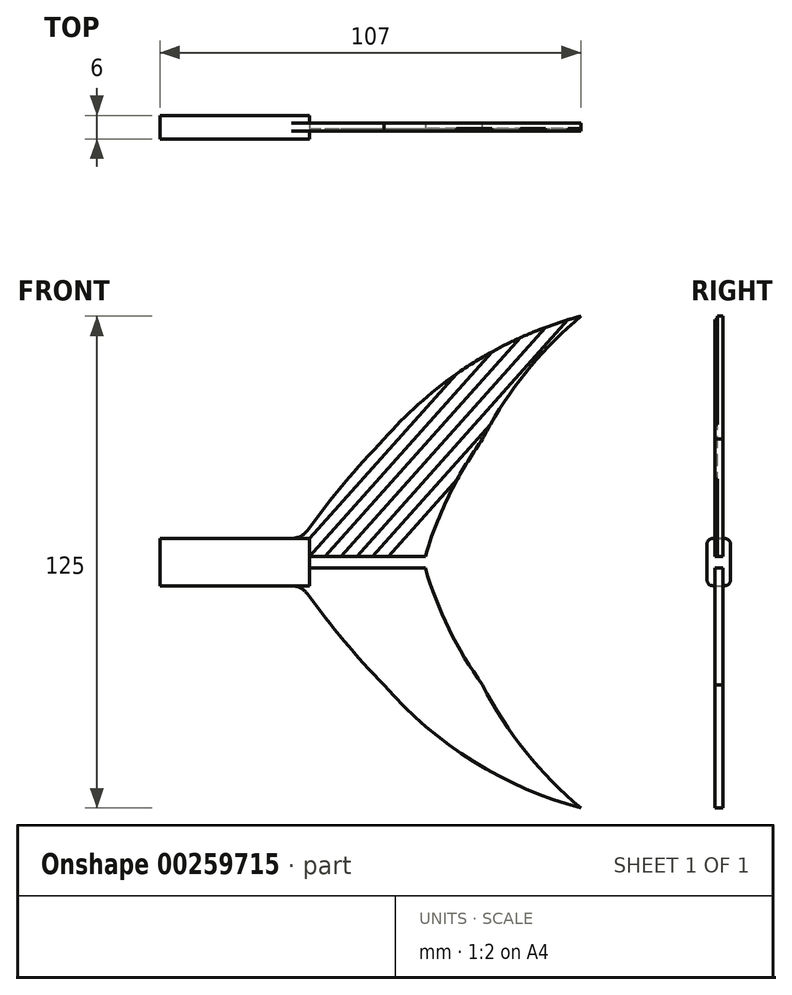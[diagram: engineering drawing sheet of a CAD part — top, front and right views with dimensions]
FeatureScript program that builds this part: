
annotation { "Feature Type Name" : "Feature", "Feature Type Description" : "" }
export const myFeature = defineFeature(function(context is Context, id is Id, definition is map)
    precondition{}
    {
        {
            var Q0;
            Q0=qCreatedBy(makeId("Front.planeOp"),FACE);
            var sketch = newSketch(context, id + "F0", { "sketchPlane" : qUnion([Q0])});
            skLineSegment(sketch, "E0", {"start": v(0, 0) * mm, "end": v(35, 0) * mm});
            skLineSegment(sketch, "E1", {"start": v(25, 31.25) * mm, "end": v(50, 31.25) * mm});
            skPoint(sketch, "E2", {"position": v(75, 62.5) * mm});
            skArc(sketch, "E3", {"start": v(25, 31.25) * mm, "mid": v(11.72, 16.25) * mm, "end": v(0, 0) * mm});
            skArc(sketch, "E4", {"start": v(75, 62.5) * mm, "mid": v(47.64, 50.64) * mm, "end": v(25, 31.25) * mm});
            skArc(sketch, "E5", {"start": v(75, 62.5) * mm, "mid": v(60.92, 48.14) * mm, "end": v(50, 31.25) * mm});
            skArc(sketch, "E6", {"start": v(50, 31.25) * mm, "mid": v(41.14, 16.28) * mm, "end": v(35, 0) * mm});
            skSolve(sketch);
        }
        {
            var Q0;
            Q0=qSketchRegion(id+"F0",true);
            extrude(context, id + "F1", {"entities" : qUnion([Q0]), "endBound" : BoundingType.SYMMETRIC, "depth" : 2 * mm});
        }
        {
            var Q0;
            Q0=makeQuery(id+"F1.opExtrude","SWEPT_BODY",BODY,{"disambiguationData":[OSD([sQuery(id+"F0.wireOp",EDGE,"E0"),sQuery(id+"F0.wireOp",EDGE,"E3"),sQuery(id+"F0.wireOp",EDGE,"E4"),sQuery(id+"F0.wireOp",EDGE,"E5"),sQuery(id+"F0.wireOp",EDGE,"E6")])]});
            var Q1;
            Q1=qCreatedBy(makeId("Top.planeOp"),FACE);
            mirror(context, id + "F2", {"operationType" : NewBodyOperationType.ADD, "entities" : qUnion([Q0]), "mirrorPlane" : qUnion([Q1])});
        }
        {
            var Q0;
            Q0=qCreatedBy(makeId("Front.planeOp"),FACE);
            var sketch = newSketch(context, id + "F3", { "sketchPlane" : qUnion([Q0])});
            skLineSegment(sketch, "E7.bottom", {"start": v(6, 6) * mm, "end": v(-32, 6) * mm});
            skLineSegment(sketch, "E7.top", {"start": v(6, -6) * mm, "end": v(-32, -6) * mm});
            skLineSegment(sketch, "E7.left", {"start": v(6, 6) * mm, "end": v(6, -6) * mm});
            skLineSegment(sketch, "E7.right", {"start": v(-32, 6) * mm, "end": v(-32, -6) * mm});
            skSolve(sketch);
        }
        {
            var Q0;
            Q0=makeQuery(id+"F3.imprint","IMPRINT",FACE,{"disambiguationData":[TD([[makeQuery(id+"F3.imprint","IMPRINT",EDGE,{"derivedFrom":sQuery(id+"F3.wireOp",EDGE,"E7.bottom")}),1.0]])]});
            extrude(context, id + "F4", {"entities" : qUnion([Q0]), "operationType" : NewBodyOperationType.ADD, "endBound" : BoundingType.SYMMETRIC, "depth" : 6 * mm});
        }
        {
            var Q0;
            Q0=makeQuery(id+"F4.opExtrude","CAP_EDGE",EDGE,{"disambiguationData":[OSD([sQuery(id+"F3.wireOp",EDGE,"E7.bottom")])],"isStart":true});
            var Q1;
            Q1=makeQuery(id+"F4.opExtrude","CAP_EDGE",EDGE,{"disambiguationData":[OSD([sQuery(id+"F3.wireOp",EDGE,"E7.bottom")])],"isStart":false});
            var Q2;
            Q2=makeQuery(id+"F4.opExtrude","CAP_EDGE",EDGE,{"disambiguationData":[OSD([sQuery(id+"F3.wireOp",EDGE,"E7.top")])],"isStart":false});
            var Q3;
            Q3=makeQuery(id+"F4.opExtrude","CAP_EDGE",EDGE,{"disambiguationData":[OSD([sQuery(id+"F3.wireOp",EDGE,"E7.top")])],"isStart":true});
            fillet(context, id + "F5", {"entities" : qUnion([Q0, Q1, Q2, Q3]), "radius" : 1.5 * mm, "tangentPropagation" : true, "allowEdgeOverflow" : false});
        }
        {
            var Q0;
            {var subQ0=makeQuery(id+"F1.opExtrude","CAP_FACE",FACE,{"disambiguationData":[OSD([sQuery(id+"F0.wireOp",EDGE,"E0"),sQuery(id+"F0.wireOp",EDGE,"E3"),sQuery(id+"F0.wireOp",EDGE,"E4"),sQuery(id+"F0.wireOp",EDGE,"E5"),sQuery(id+"F0.wireOp",EDGE,"E6")])],"isStart":false});Q0=makeQuery(id+"F2.boolean.opBoolean","MERGE",FACE,{"derivedFrom":[subQ0,makeQuery(id+"F2.opPattern","COPY",FACE,{"derivedFrom":subQ0,"instanceName":"1"})]});}
            var sketch = newSketch(context, id + "F6", { "sketchPlane" : qUnion([Q0])});
            skLineSegment(sketch, "E8", {"start": v(6, 6) * mm, "end": v(43.34, 47.8) * mm});
            skLineSegment(sketch, "E9", {"start": v(6, 1.5) * mm, "end": v(52.4, 53.44) * mm});
            skLineSegment(sketch, "E10", {"start": v(10.03, 1.5) * mm, "end": v(59.66, 57.06) * mm});
            skLineSegment(sketch, "E11", {"start": v(14.05, 1.5) * mm, "end": v(66, 59.65) * mm});
            skLineSegment(sketch, "E12", {"start": v(18.07, 1.5) * mm, "end": v(71.74, 61.58) * mm});
            skLineSegment(sketch, "E13", {"start": v(22.1, 1.5) * mm, "end": v(52.03, 35) * mm});
            skLineSegment(sketch, "E14", {"start": v(26.12, 1.5) * mm, "end": v(43.6, 21.06) * mm});
            skLineSegment(sketch, "E15", {"start": v(6, 1.5) * mm, "end": v(35.43, 1.5) * mm});
            skSolve(sketch);
        }
        {
            var Q0;
            {var subQ0=sQuery(id+"F6.wireOp",EDGE,"E8");Q0=makeQuery(id+"F6.imprint","IMPRINT",FACE,{"disambiguationData":[TD([[makeQuery(id+"F6.imprint","IMPRINT",EDGE,{"derivedFrom":subQ0}),-1.0]])]});}
            var Q1;
            {var subQ0=sQuery(id+"F6.wireOp",EDGE,"E10");Q1=makeQuery(id+"F6.imprint","IMPRINT",FACE,{"disambiguationData":[TD([[makeQuery(id+"F6.imprint","IMPRINT",EDGE,{"derivedFrom":subQ0}),-1.0]])]});}
            var Q2;
            {var subQ3=sQuery(id+"F6.wireOp",EDGE,"E12");Q2=makeQuery(id+"F6.imprint","IMPRINT",FACE,{"disambiguationData":[TD([[makeQuery(id+"F6.imprint","IMPRINT",EDGE,{"derivedFrom":subQ3}),-1.0]])]});}
            var Q3;
            {var subQ3=sQuery(id+"F6.wireOp",EDGE,"E14");Q3=makeQuery(id+"F6.imprint","IMPRINT",FACE,{"disambiguationData":[TD([[makeQuery(id+"F6.imprint","IMPRINT",EDGE,{"derivedFrom":subQ3}),-1.0]])]});}
            extrude(context, id + "F7", {"entities" : qUnion([Q0, Q1, Q2, Q3]), "operationType" : NewBodyOperationType.REMOVE, "oppositeDirection" : true, "depth" : 0.7 * mm});
        }
        {
            var Q0;
            {var subQ1=sQuery(id+"F0.wireOp",EDGE,"E5");var subQ2=makeQuery(id+"F1.opExtrude","SWEPT_FACE",FACE,{"disambiguationData":[OSD([subQ1])]});var subQ4=sQuery(id+"F0.wireOp",EDGE,"E4");var subQ5=makeQuery(id+"F1.opExtrude","SWEPT_FACE",FACE,{"disambiguationData":[OSD([subQ4])]});var subQ14=sQuery(id+"F0.wireOp",EDGE,"E6");var subQ15=sQuery(id+"F0.wireOp",EDGE,"E3");var subQ16=sQuery(id+"F0.wireOp",EDGE,"E0");var subQ17=makeQuery(id+"F1.opExtrude","CAP_FACE",FACE,{"disambiguationData":[OSD([subQ16,subQ15,subQ4,subQ1,subQ14])],"isStart":false});var subQ18=makeQuery(id+"F2.boolean.opBoolean","MERGE",FACE,{"derivedFrom":[subQ17,makeQuery(id+"F2.opPattern","COPY",FACE,{"derivedFrom":subQ17,"instanceName":"1"})]});Q0=makeQuery(id+"Fphz1cvsCfrwwfK_1.1.F7.boolean.opBoolean","SPLIT",FACE,{"disambiguationData":[TD([subQ5])],"derivedFrom":makeQuery(id+"F7.boolean.opBoolean","SPLIT",FACE,{"disambiguationData":[TD([subQ2])],"derivedFrom":subQ18})});}
            var sketch = newSketch(context, id + "F8", { "sketchPlane" : qUnion([Q0])});
            skLineSegment(sketch, "E16.bottom", {"start": v(6, 1.5) * mm, "end": v(36.75, 1.5) * mm});
            skLineSegment(sketch, "E16.top", {"start": v(6, -1.5) * mm, "end": v(36.75, -1.5) * mm});
            skLineSegment(sketch, "E16.left", {"start": v(6, 1.5) * mm, "end": v(6, -1.5) * mm});
            skLineSegment(sketch, "E16.right", {"start": v(36.75, 1.5) * mm, "end": v(36.75, -1.5) * mm});
            skSolve(sketch);
        }
        {
            var Q0;
            {var subQ13=sQuery(id+"F8.wireOp",EDGE,"E16.left");Q0=makeQuery(id+"F8.imprint","IMPRINT",FACE,{"disambiguationData":[TD([[makeQuery(id+"F8.imprint","IMPRINT",EDGE,{"derivedFrom":subQ13}),-1.0]])]});}
            extrude(context, id + "F9", {"entities" : qUnion([Q0]), "operationType" : NewBodyOperationType.REMOVE, "endBound" : BoundingType.SYMMETRIC, "oppositeDirection" : true, "depth" : 25 * mm});
        }
        {
            var Q0;
            Q0=makeQuery(id+"F4.boolean.opBoolean","INTERSECT",EDGE,{"derivedFrom":[makeQuery(id+"F1.opExtrude","SWEPT_FACE",FACE,{"disambiguationData":[OSD([sQuery(id+"F0.wireOp",EDGE,"E3")])]}),makeQuery(id+"F4.opExtrude","SWEPT_FACE",FACE,{"disambiguationData":[OSD([sQuery(id+"F3.wireOp",EDGE,"E7.bottom")])]})]});
            var Q1;
            Q1=makeQuery(id+"F4.boolean.opBoolean","INTERSECT",EDGE,{"derivedFrom":[makeQuery(id+"F2.opPattern","COPY",FACE,{"derivedFrom":makeQuery(id+"F1.opExtrude","SWEPT_FACE",FACE,{"disambiguationData":[OSD([sQuery(id+"F0.wireOp",EDGE,"E3")])]}),"instanceName":"1"}),makeQuery(id+"F4.opExtrude","SWEPT_FACE",FACE,{"disambiguationData":[OSD([sQuery(id+"F3.wireOp",EDGE,"E7.top")])]})]});
            fillet(context, id + "F10", {"entities" : qUnion([Q0, Q1]), "radius" : 5 * mm, "tangentPropagation" : true, "allowEdgeOverflow" : false});
        }
    });
